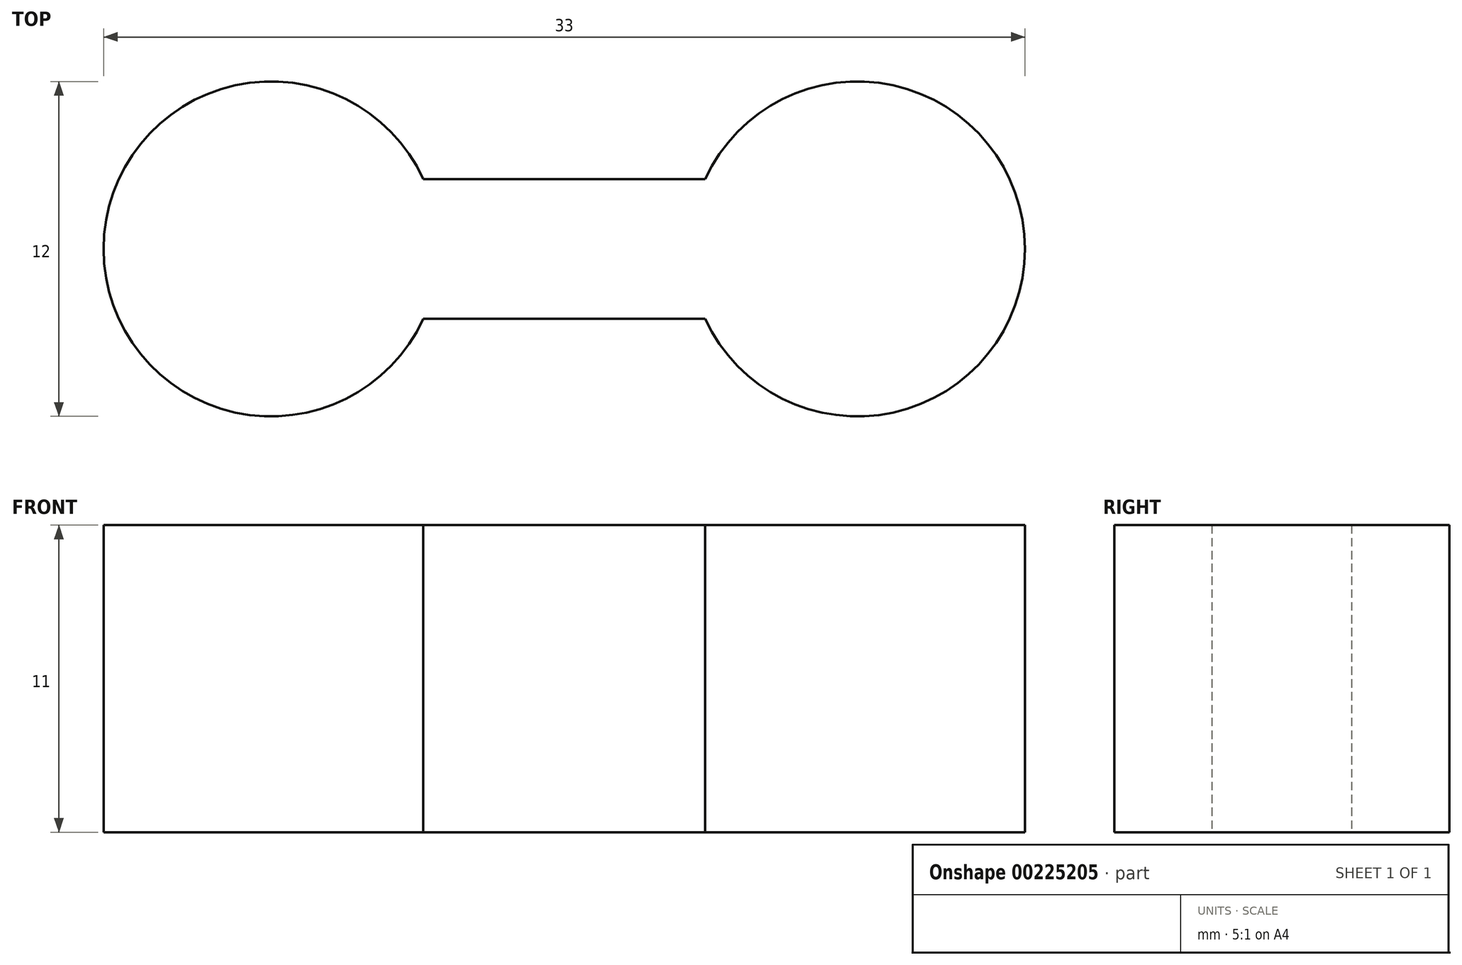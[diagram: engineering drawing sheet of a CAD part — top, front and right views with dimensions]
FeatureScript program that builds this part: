
annotation { "Feature Type Name" : "Feature", "Feature Type Description" : "" }
export const myFeature = defineFeature(function(context is Context, id is Id, definition is map)
    precondition{}
    {
        {
            var Q0;
            Q0=qCreatedBy(makeId("Top.planeOp"),FACE);
            var sketch = newSketch(context, id + "F0", { "sketchPlane" : qUnion([Q0])});
            skArc(sketch, "E0", {"start": v(5.05, -2.5) * mm, "mid": v(16.5, 0) * mm, "end": v(5.05, 2.5) * mm});
            skArc(sketch, "E1.MirrorC", {"start": v(-5.05, -2.5) * mm, "mid": v(-16.5, 0) * mm, "end": v(-5.05, 2.5) * mm});
            skLineSegment(sketch, "E2.bottom", {"start": v(5.05, -2.5) * mm, "end": v(-5.05, -2.5) * mm});
            skLineSegment(sketch, "E2.top", {"start": v(5.05, 2.5) * mm, "end": v(-5.05, 2.5) * mm});
            skPoint(sketch, "E2.middle", {"position": v(0, 0) * mm});
            skPoint(sketch, "E3.orphan", {"position": v(7.48, 2.5) * mm});
            skPoint(sketch, "E4.orphan", {"position": v(7.48, -2.5) * mm});
            skPoint(sketch, "E2.right.start.orphan", {"position": v(-7.48, -2.5) * mm});
            skPoint(sketch, "E5.orphan", {"position": v(-7.48, 2.5) * mm});
            skSolve(sketch);
        }
        {
            var Q0;
            Q0=makeQuery(id+"F0.imprint","IMPRINT",FACE,{"disambiguationData":[TD([[makeQuery(id+"F0.imprint","IMPRINT",EDGE,{"derivedFrom":sQuery(id+"F0.wireOp",EDGE,"E0")}),1.0]])]});
            extrude(context, id + "F1", {"entities" : qUnion([Q0]), "depth" : 11 * mm});
        }
    });
